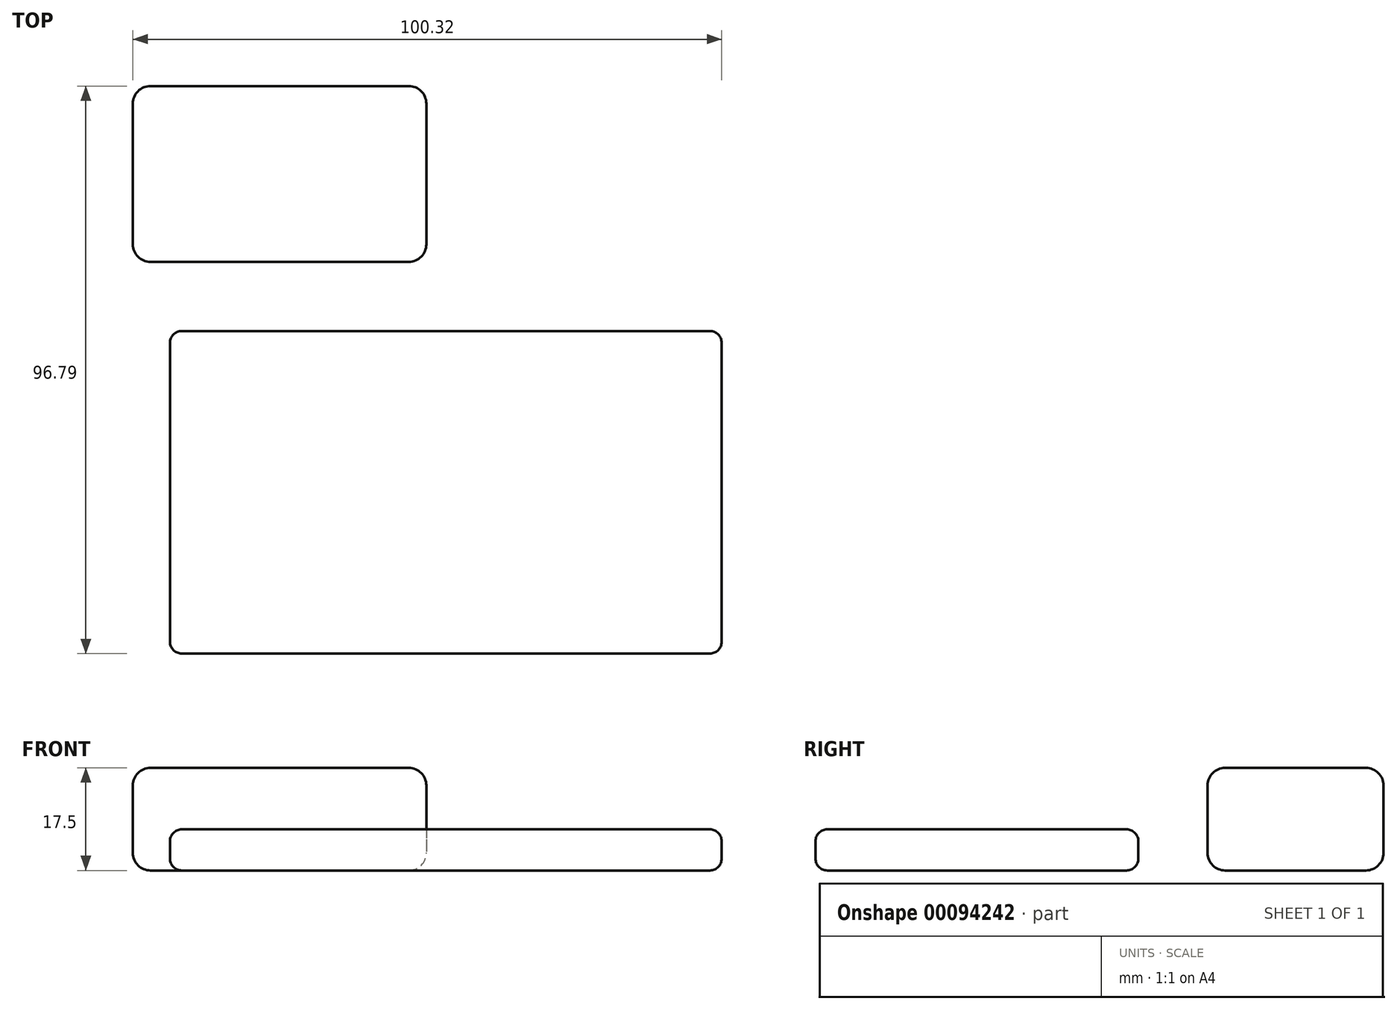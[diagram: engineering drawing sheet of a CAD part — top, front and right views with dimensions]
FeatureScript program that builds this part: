
annotation { "Feature Type Name" : "Feature", "Feature Type Description" : "" }
export const myFeature = defineFeature(function(context is Context, id is Id, definition is map)
    precondition{}
    {
        {
            var Q0;
            Q0=qCreatedBy(makeId("Top.planeOp"),FACE);
            var sketch = newSketch(context, id + "F0", { "sketchPlane" : qUnion([Q0])});
            skLineSegment(sketch, "E0.bottom", {"start": v(25, -15) * mm, "end": v(-25, -15) * mm});
            skLineSegment(sketch, "E0.top", {"start": v(25, 15) * mm, "end": v(-25, 15) * mm});
            skLineSegment(sketch, "E0.left", {"start": v(25, -15) * mm, "end": v(25, 15) * mm});
            skLineSegment(sketch, "E0.right", {"start": v(-25, -15) * mm, "end": v(-25, 15) * mm});
            skPoint(sketch, "E0.middle", {"position": v(0, 0) * mm});
            skSolve(sketch);
        }
        {
            var Q0;
            Q0=makeQuery(id+"F0.imprint","IMPRINT",FACE,{"disambiguationData":[TD([[makeQuery(id+"F0.imprint","IMPRINT",EDGE,{"derivedFrom":sQuery(id+"F0.wireOp",EDGE,"E0.bottom")}),-1.0]])]});
            extrude(context, id + "F1", {"entities" : qUnion([Q0]), "depth" : 17.5 * mm});
        }
        {
            var Q0;
            Q0=makeQuery(id+"F1.opExtrude","CAP_FACE",FACE,{"disambiguationData":[OSD([sQuery(id+"F0.wireOp",EDGE,"E0.bottom"),sQuery(id+"F0.wireOp",EDGE,"E0.top"),sQuery(id+"F0.wireOp",EDGE,"E0.left"),sQuery(id+"F0.wireOp",EDGE,"E0.right")])],"isStart":false});
            var Q1;
            Q1=makeQuery(id+"F1.opExtrude","SWEPT_FACE",FACE,{"disambiguationData":[OSD([sQuery(id+"F0.wireOp",EDGE,"E0.bottom")])]});
            var Q2;
            Q2=makeQuery(id+"F1.opExtrude","SWEPT_EDGE",EDGE,{"disambiguationData":[OSD([sQuery(id+"F0.wireOp",EDGE,"E0.bottom"),sQuery(id+"F0.wireOp",EDGE,"E0.left")])]});
            var Q3;
            Q3=makeQuery(id+"F1.opExtrude","CAP_FACE",FACE,{"disambiguationData":[OSD([sQuery(id+"F0.wireOp",EDGE,"E0.bottom"),sQuery(id+"F0.wireOp",EDGE,"E0.top"),sQuery(id+"F0.wireOp",EDGE,"E0.left"),sQuery(id+"F0.wireOp",EDGE,"E0.right")])],"isStart":true});
            var Q4;
            Q4=makeQuery(id+"F1.opExtrude","SWEPT_EDGE",EDGE,{"disambiguationData":[OSD([sQuery(id+"F0.wireOp",EDGE,"E0.bottom"),sQuery(id+"F0.wireOp",EDGE,"E0.right")])]});
            var Q5;
            Q5=makeQuery(id+"F1.opExtrude","SWEPT_EDGE",EDGE,{"disambiguationData":[OSD([sQuery(id+"F0.wireOp",EDGE,"E0.top"),sQuery(id+"F0.wireOp",EDGE,"E0.left")])]});
            var Q6;
            Q6=makeQuery(id+"F1.opExtrude","SWEPT_FACE",FACE,{"disambiguationData":[OSD([sQuery(id+"F0.wireOp",EDGE,"E0.top")])]});
            var Q7;
            Q7=makeQuery(id+"F1.opExtrude","SWEPT_FACE",FACE,{"disambiguationData":[OSD([sQuery(id+"F0.wireOp",EDGE,"E0.left")])]});
            var Q8;
            Q8=makeQuery(id+"F1.opExtrude","CAP_EDGE",EDGE,{"disambiguationData":[OSD([sQuery(id+"F0.wireOp",EDGE,"E0.bottom")])],"isStart":true});
            var Q9;
            Q9=makeQuery(id+"F1.opExtrude","SWEPT_FACE",FACE,{"disambiguationData":[OSD([sQuery(id+"F0.wireOp",EDGE,"E0.right")])]});
            var Q10;
            Q10=makeQuery(id+"F1.opExtrude","CAP_EDGE",EDGE,{"disambiguationData":[OSD([sQuery(id+"F0.wireOp",EDGE,"E0.top")])],"isStart":false});
            var Q11;
            Q11=makeQuery(id+"F1.opExtrude","CAP_EDGE",EDGE,{"disambiguationData":[OSD([sQuery(id+"F0.wireOp",EDGE,"E0.left")])],"isStart":true});
            var Q12;
            Q12=makeQuery(id+"F1.opExtrude","CAP_EDGE",EDGE,{"disambiguationData":[OSD([sQuery(id+"F0.wireOp",EDGE,"E0.left")])],"isStart":false});
            var Q13;
            Q13=makeQuery(id+"F1.opExtrude","CAP_EDGE",EDGE,{"disambiguationData":[OSD([sQuery(id+"F0.wireOp",EDGE,"E0.right")])],"isStart":false});
            var Q14;
            Q14=makeQuery(id+"F1.opExtrude","SWEPT_EDGE",EDGE,{"disambiguationData":[OSD([sQuery(id+"F0.wireOp",EDGE,"E0.top"),sQuery(id+"F0.wireOp",EDGE,"E0.right")])]});
            var Q15;
            Q15=makeQuery(id+"F1.opExtrude","CAP_EDGE",EDGE,{"disambiguationData":[OSD([sQuery(id+"F0.wireOp",EDGE,"E0.bottom")])],"isStart":false});
            var Q16;
            Q16=makeQuery(id+"F1.opExtrude","CAP_EDGE",EDGE,{"disambiguationData":[OSD([sQuery(id+"F0.wireOp",EDGE,"E0.top")])],"isStart":true});
            var Q17;
            Q17=makeQuery(id+"F1.opExtrude","CAP_EDGE",EDGE,{"disambiguationData":[OSD([sQuery(id+"F0.wireOp",EDGE,"E0.right")])],"isStart":true});
            fillet(context, id + "F2", {"entities" : qUnion([Q0, Q1, Q2, Q3, Q4, Q5, Q6, Q7, Q8, Q9, Q10, Q11, Q12, Q13, Q14, Q15, Q16, Q17]), "radius" : 3 * mm, "tangentPropagation" : true, "allowEdgeOverflow" : false});
        }
        {
            var Q0;
            Q0=qCreatedBy(makeId("Top.planeOp"),FACE);
            var sketch = newSketch(context, id + "F3", { "sketchPlane" : qUnion([Q0])});
            skLineSegment(sketch, "E1.bottom", {"start": v(-18.68, -26.79) * mm, "end": v(75.32, -26.79) * mm});
            skLineSegment(sketch, "E1.top", {"start": v(-18.68, -81.79) * mm, "end": v(75.32, -81.79) * mm});
            skLineSegment(sketch, "E1.left", {"start": v(-18.68, -26.79) * mm, "end": v(-18.68, -81.79) * mm});
            skLineSegment(sketch, "E1.right", {"start": v(75.32, -26.79) * mm, "end": v(75.32, -81.79) * mm});
            skSolve(sketch);
        }
        {
            var Q0;
            Q0=makeQuery(id+"F3.imprint","IMPRINT",FACE,{"disambiguationData":[TD([[makeQuery(id+"F3.imprint","IMPRINT",EDGE,{"derivedFrom":sQuery(id+"F3.wireOp",EDGE,"E1.bottom")}),-1.0]])]});
            extrude(context, id + "F4", {"entities" : qUnion([Q0]), "depth" : 7 * mm});
        }
        {
            var Q0;
            Q0=makeQuery(id+"F4.opExtrude","CAP_EDGE",EDGE,{"disambiguationData":[OSD([sQuery(id+"F3.wireOp",EDGE,"E1.top")])],"isStart":false});
            var Q1;
            Q1=makeQuery(id+"F4.opExtrude","CAP_EDGE",EDGE,{"disambiguationData":[OSD([sQuery(id+"F3.wireOp",EDGE,"E1.top")])],"isStart":true});
            var Q2;
            Q2=makeQuery(id+"F4.opExtrude","CAP_EDGE",EDGE,{"disambiguationData":[OSD([sQuery(id+"F3.wireOp",EDGE,"E1.bottom")])],"isStart":true});
            var Q3;
            Q3=makeQuery(id+"F4.opExtrude","CAP_EDGE",EDGE,{"disambiguationData":[OSD([sQuery(id+"F3.wireOp",EDGE,"E1.bottom")])],"isStart":false});
            var Q4;
            Q4=makeQuery(id+"F4.opExtrude","SWEPT_EDGE",EDGE,{"disambiguationData":[OSD([sQuery(id+"F3.wireOp",EDGE,"E1.bottom"),sQuery(id+"F3.wireOp",EDGE,"E1.right")])]});
            var Q5;
            Q5=makeQuery(id+"F4.opExtrude","SWEPT_EDGE",EDGE,{"disambiguationData":[OSD([sQuery(id+"F3.wireOp",EDGE,"E1.top"),sQuery(id+"F3.wireOp",EDGE,"E1.right")])]});
            var Q6;
            Q6=makeQuery(id+"F4.opExtrude","CAP_EDGE",EDGE,{"disambiguationData":[OSD([sQuery(id+"F3.wireOp",EDGE,"E1.right")])],"isStart":false});
            var Q7;
            Q7=makeQuery(id+"F4.opExtrude","CAP_EDGE",EDGE,{"disambiguationData":[OSD([sQuery(id+"F3.wireOp",EDGE,"E1.right")])],"isStart":true});
            var Q8;
            Q8=makeQuery(id+"F4.opExtrude","CAP_EDGE",EDGE,{"disambiguationData":[OSD([sQuery(id+"F3.wireOp",EDGE,"E1.left")])],"isStart":false});
            var Q9;
            Q9=makeQuery(id+"F4.opExtrude","CAP_EDGE",EDGE,{"disambiguationData":[OSD([sQuery(id+"F3.wireOp",EDGE,"E1.left")])],"isStart":true});
            var Q10;
            Q10=makeQuery(id+"F4.opExtrude","SWEPT_EDGE",EDGE,{"disambiguationData":[OSD([sQuery(id+"F3.wireOp",EDGE,"E1.bottom"),sQuery(id+"F3.wireOp",EDGE,"E1.left")])]});
            var Q11;
            Q11=makeQuery(id+"F4.opExtrude","SWEPT_EDGE",EDGE,{"disambiguationData":[OSD([sQuery(id+"F3.wireOp",EDGE,"E1.top"),sQuery(id+"F3.wireOp",EDGE,"E1.left")])]});
            fillet(context, id + "F5", {"entities" : qUnion([Q0, Q1, Q2, Q3, Q4, Q5, Q6, Q7, Q8, Q9, Q10, Q11]), "radius" : 2 * mm, "tangentPropagation" : true, "allowEdgeOverflow" : false});
        }
    });
